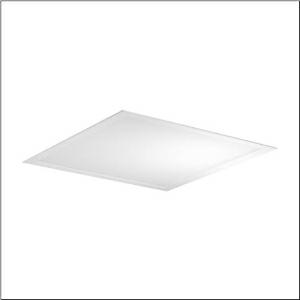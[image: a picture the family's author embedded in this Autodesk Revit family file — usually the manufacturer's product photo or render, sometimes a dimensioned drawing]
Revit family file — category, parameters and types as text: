
# Revit family: apollon_21_square_51mq11w72414m
name_source: partatom
category: Lighting Fixtures
units: mm (PartAtom-declared; Revit-internal decimal feet)

## family parameters
Cut with Voids When Loaded = No
Host = Face
Light Source = No
Part Type = Normal
Room Calculation Point = No
Round Connector Dimension = Use Diameter
Shared = No

## types (1)
- Apollon 21 square (1 x LED, 4200 lm, 23.3 W, 4000K)
    Apparent Load = 23 VA
    CIE Flux Codes = 60 87 97 100 100
    Color Rendering = 80
    Color Temperature = 4000K
    Default Elevation = 1800 mm
    Description = Apollon 21 square, office luminaire, primary optical cover: micro prismatic cover, of PMMA, CAT 2 (L<= 3000cd/m²), light emission: direct distribution, primary light characteristic: symmetric, installation type: lay-in mounting, recessed, LED, rated luminous flux: 4.200lm, luminous efficacy: 180lm/W, light colour: 840, colour temperature: 4000K, control gear: ON/OFF, with terminal, 3-pole, mains connection: 220..240V, AC/DC, 0/50..60Hz, rated input power: 23.3W, suitable for self-contained emergency lighting element 59MQE002602A with integrated self-test function according to EN 60598-2-22, housing, of aluminium, coated, traffic white (RAL 9016), module: M625, length: 620mm, width: 620mm, height: 55mm, housing upper side, of sheet steel, galvanised, protection rating (complete): IP20, protection rating (lamp compartment, on room side): IP50, insulation class (complete): insulation class II (safety insulation), certification: CE, ENEC, impact resistance: IK03, permissible operating ambient temperature: -20..+45°C, standard: EN 60598-2-22, corresponds to IFS (International Featured Standards) requirements for safety and quality in the food industry, packaging unit: set of 5
    Height = 0 mm  [stored 0 ft]
    Lamp = 1 x LED
    Lamp Light Flux = 4200 lm
    Lamp Power = 23.3 W
    Lamp count = 1
    Length = 620 mm
    Luminous efficacy = 180 lm/W
    Manufacturer = Siteco
    ModVariant = No
    Model = 51MQ11W72414M
    Mounting Place = Ceiling
    Mounting Type = Recessed
    Number of Poles = 1
    OnlyDefault = Yes
    Power Factor = 1
    Product Name = Apollon 21 square
    Product group = office luminaire | ceiling recessed
    ProductGroupID = 400
    Protection Class = Protection class II
    Protection Degree = IP 20
    RLX_Detail_Level = 1
    RLX_Emergency_Light_Flux = 0 lm
    RLX_Emergency_Type = 0
    RLX_Emergency_Type_DB = No
    RlxData = <blob elided: 13297 chars, md5=39d0642b>
    Socket = socket
    Standby Power = 0 W
    System Light Flux = 4200 lm
    System Power = 23 W
    Type Comments = Product without accessories
    Type Image = l_1291054.jpg
    URL = http://relux.com
    VarID = ---
    Voltage = 0 V
    Weight = 0.00 kg
    Width = 620 mm

note: [stored X ft] marks values corroborated as IEEE doubles in the binary element streams (Revit-internal decimal feet)

## geometry (parser evidence)
native form markers: Sweep x10
no freeform markers — native parametric forms only
